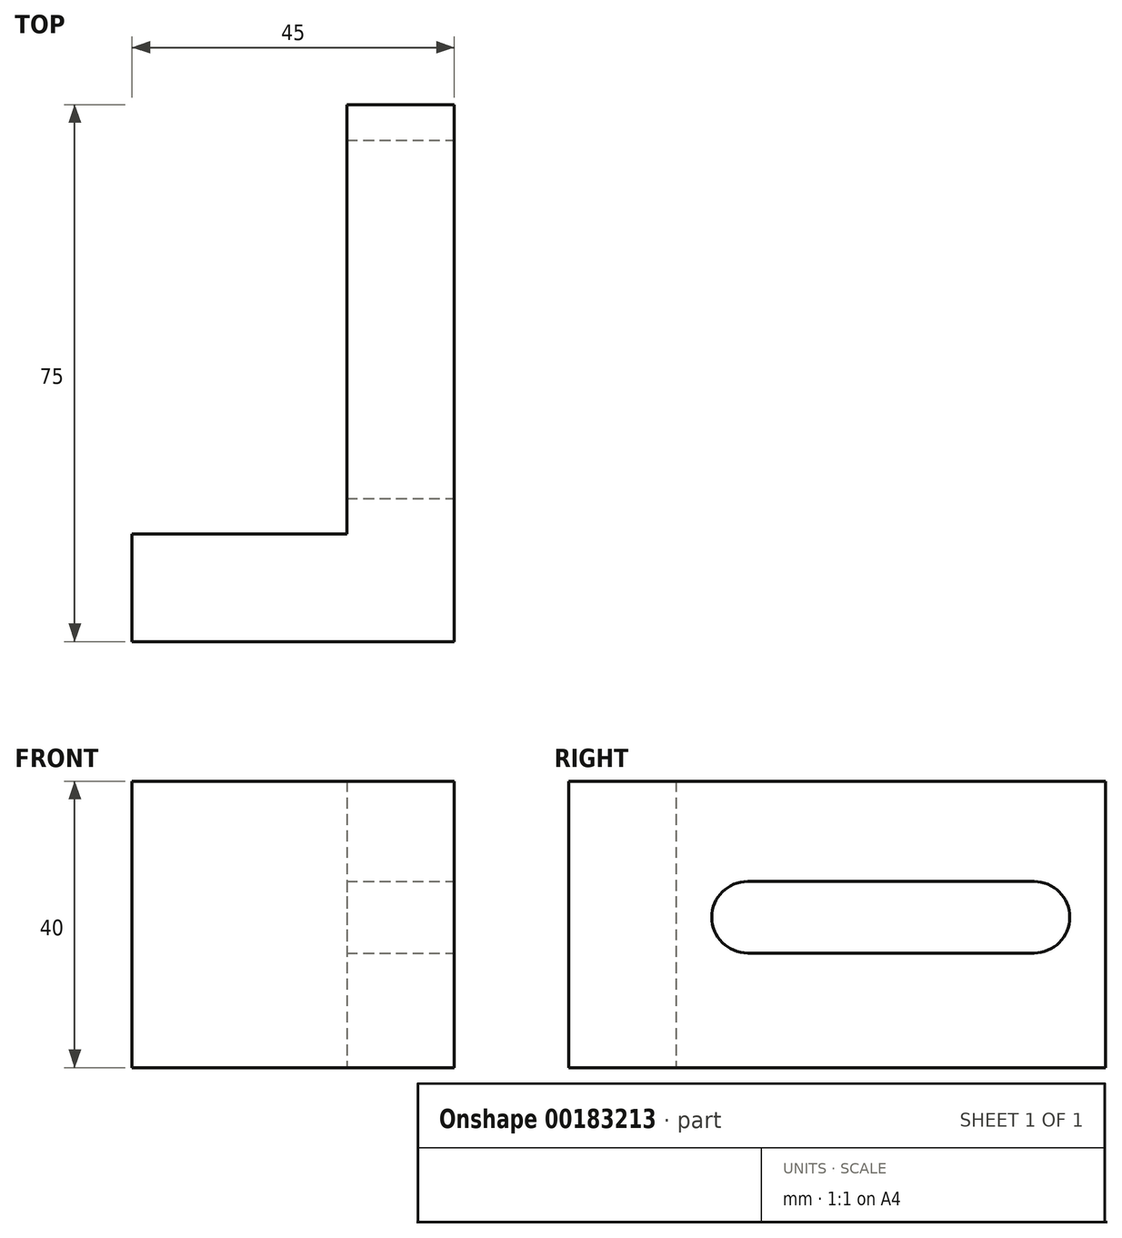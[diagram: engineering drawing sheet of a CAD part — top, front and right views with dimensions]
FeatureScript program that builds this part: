
annotation { "Feature Type Name" : "Feature", "Feature Type Description" : "" }
export const myFeature = defineFeature(function(context is Context, id is Id, definition is map)
    precondition{}
    {
        {
            var Q0;
            Q0=qCreatedBy(makeId("Top.planeOp"),FACE);
            var sketch = newSketch(context, id + "F0", { "sketchPlane" : qUnion([Q0])});
            skLineSegment(sketch, "E0.bottom", {"start": v(0, 0) * mm, "end": v(-45, 0) * mm});
            skLineSegment(sketch, "E0.top", {"start": v(-15, 15) * mm, "end": v(-45, 15) * mm});
            skLineSegment(sketch, "E0.right", {"start": v(-45, 0) * mm, "end": v(-45, 15) * mm});
            skLineSegment(sketch, "E1.top", {"start": v(0, 75) * mm, "end": v(-15, 75) * mm});
            skLineSegment(sketch, "E1.right", {"start": v(-15, 15) * mm, "end": v(-15, 75) * mm});
            skLineSegment(sketch, "E2", {"start": v(0, 75) * mm, "end": v(0, 0) * mm});
            skSolve(sketch);
        }
        {
            var Q0;
            Q0=makeQuery(id+"F0.imprint","IMPRINT",FACE,{"disambiguationData":[TD([[makeQuery(id+"F0.imprint","IMPRINT",EDGE,{"derivedFrom":sQuery(id+"F0.wireOp",EDGE,"E0.bottom")}),-1.0]])]});
            extrude(context, id + "F1", {"entities" : qUnion([Q0]), "depth" : 40 * mm});
        }
        {
            var Q0;
            Q0=makeQuery(id+"F1.opExtrude","SWEPT_FACE",FACE,{"disambiguationData":[OSD([sQuery(id+"F0.wireOp",EDGE,"E2")])]});
            var sketch = newSketch(context, id + "F2", { "sketchPlane" : qUnion([Q0])});
            skLineSegment(sketch, "E3.bottom", {"start": v(25, 26) * mm, "end": v(65, 26) * mm});
            skLineSegment(sketch, "E3.top", {"start": v(25, 16) * mm, "end": v(65, 16) * mm});
            skArc(sketch, "E4", {"start": v(25, 26) * mm, "mid": v(20, 21) * mm, "end": v(25, 16) * mm});
            skArc(sketch, "E5", {"start": v(65, 16) * mm, "mid": v(70, 21) * mm, "end": v(65, 26) * mm});
            skSolve(sketch);
        }
        {
            var Q0;
            Q0=makeQuery(id+"F2.imprint","IMPRINT",FACE,{"disambiguationData":[TD([[makeQuery(id+"F2.imprint","IMPRINT",EDGE,{"derivedFrom":sQuery(id+"F2.wireOp",EDGE,"E3.bottom")}),-1.0]])]});
            extrude(context, id + "F3", {"entities" : qUnion([Q0]), "operationType" : NewBodyOperationType.REMOVE, "endBound" : BoundingType.THROUGH_ALL, "oppositeDirection" : true, "depth" : 25 * mm});
        }
    });
